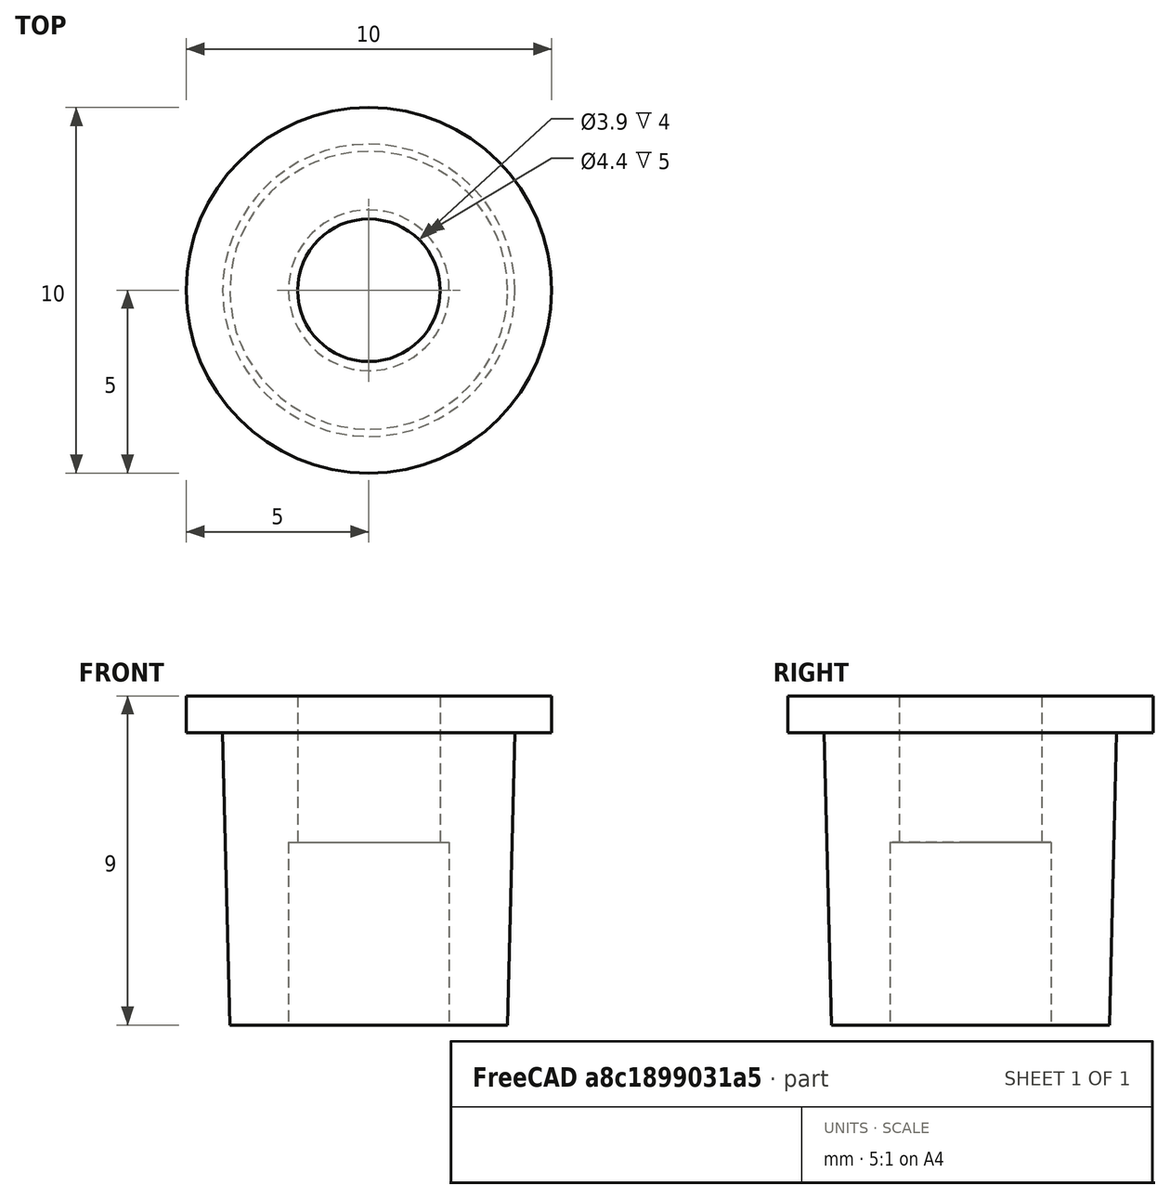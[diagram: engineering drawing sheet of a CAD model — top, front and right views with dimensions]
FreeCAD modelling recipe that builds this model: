
FCSTD DOCUMENT  (FreeCAD 0.16R6712 (Git))
Label: pipe_adapter_v1
License: All rights reserved
LicenseURL: http://en.wikipedia.org/wiki/All_rights_reserved
objects: Sketcher::SketchObject×1, PartDesign::Revolution×1
note: 3 computed .brp shape members not serialized (recipe doc carries the construction recipe); baked Part::Feature solids carry a one-line shape summary decoded from their .brp

FEATURE [Sketcher::SketchObject] Sketch
  Placement = pos=(0,0,0) rot=(-1,0,0;4.71239rad)
  sketch-geometry (8):
    g0: LineSegment StartX=-1.95 StartY=1 StartZ=0 EndX=-1.95 EndY=-3 EndZ=0
    g1: LineSegment StartX=-1.95 StartY=-3 StartZ=0 EndX=-2.2 EndY=-3 EndZ=0
    g2: LineSegment StartX=-2.2 StartY=-3 StartZ=0 EndX=-2.2 EndY=-8 EndZ=0
    g3: LineSegment StartX=-2.2 StartY=-8 StartZ=0 EndX=-3.8 EndY=-8 EndZ=0
    g4: LineSegment StartX=-3.8 StartY=-8 StartZ=0 EndX=-4 EndY=0 EndZ=0
    g5: LineSegment StartX=-4 StartY=0 StartZ=0 EndX=-5 EndY=0 EndZ=0
    g6: LineSegment StartX=-5 StartY=0 StartZ=0 EndX=-5 EndY=1 EndZ=0
    g7: LineSegment StartX=-5 StartY=1 StartZ=0 EndX=-1.95 EndY=1 EndZ=0
  constraints (24):
    c: Vertical(g0)
    c: Coincident(g0,g1)
    c: Coincident(g1,g2)
    c: Vertical(g2)
    c: Coincident(g2,g3)
    c: Horizontal(g3)
    c: Coincident(g3,g4)
    c: PointOnObject(g4,g-1)
    c: Coincident(g4,g5)
    c: PointOnObject(g5,g-1)
    c: Coincident(g5,g6)
    c: Vertical(g6)
    c: Coincident(g6,g7)
    c: Coincident(g7,g0)
    c: Horizontal(g7)
    c: DistanceX(g0,g-1) = 1.95
    c: DistanceX(g6,g-1) = 5
    c: DistanceX(g1,g-1) = 2.2
    c: DistanceX(g4,g-1) = 4
    c: DistanceX(g3,g-1) = 3.8
    c: Horizontal(g1)
    c: DistanceY(g6,g6) = 1
    c: DistanceY(g0,g0) = 4
    c: DistanceY(g3,g4) = 8
FEATURE [PartDesign::Revolution] Revolution
  Angle = 360
  Axis = (0,0,1)
  Base = (0,0,0)
  Placement = pos=(0,0,0) rot=(-1,0,0;4.71239rad)
  ReferenceAxis = -> Sketch [V_Axis]
  Sketch = -> Sketch
